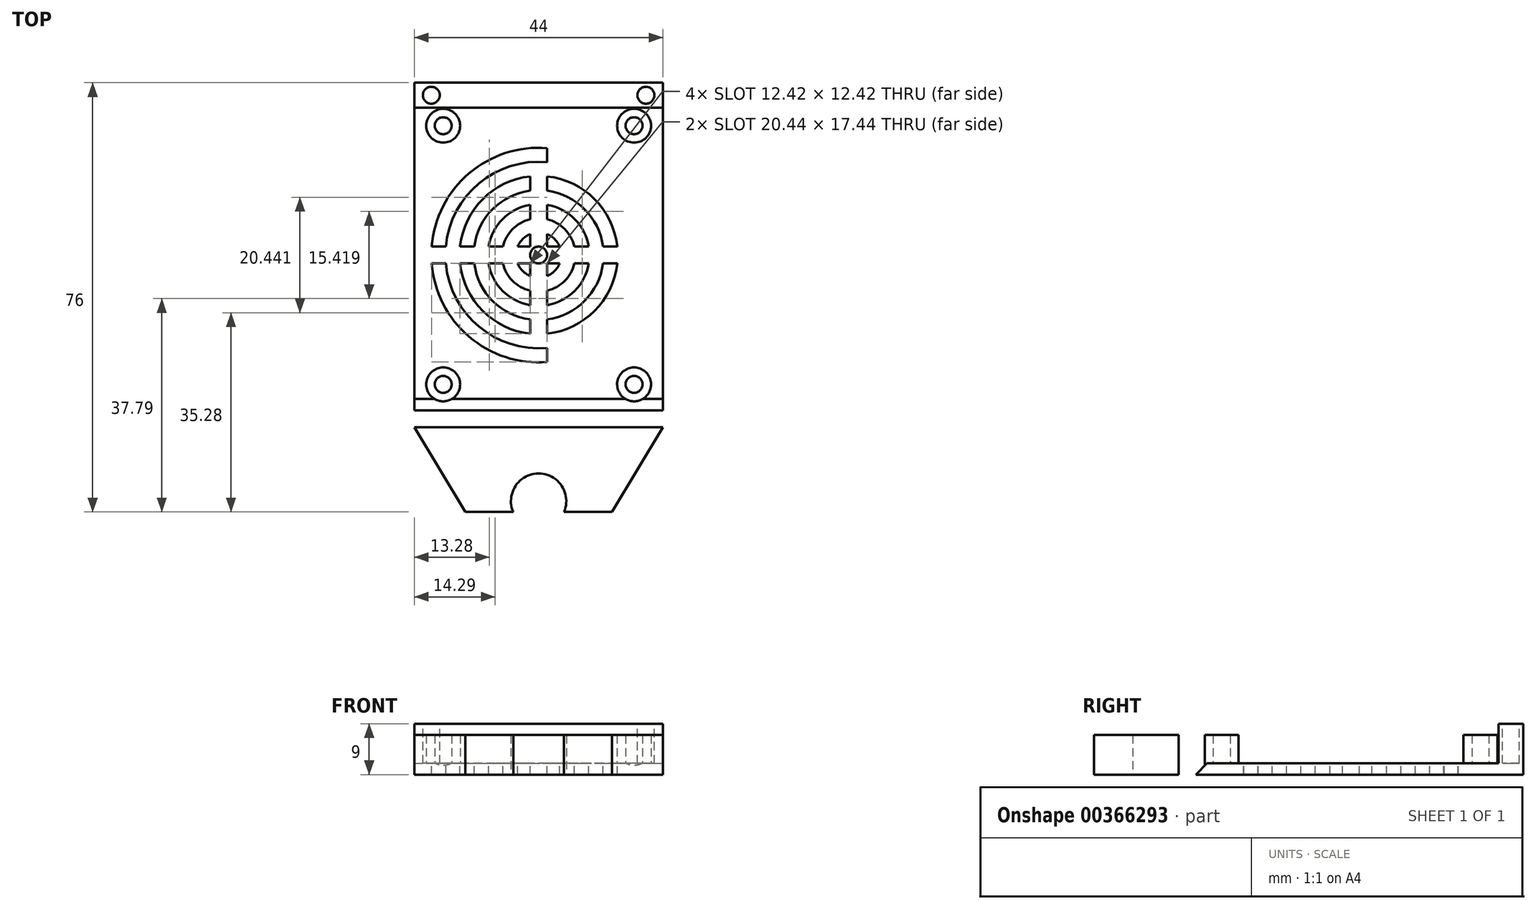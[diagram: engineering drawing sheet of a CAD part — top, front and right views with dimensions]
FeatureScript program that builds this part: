
annotation { "Feature Type Name" : "Feature", "Feature Type Description" : "" }
export const myFeature = defineFeature(function(context is Context, id is Id, definition is map)
    precondition{}
    {
        {
            var Q0;
            Q0=qCreatedBy(makeId("Top.planeOp"),FACE);
            var sketch = newSketch(context, id + "F0", { "sketchPlane" : qUnion([Q0])});
            skLineSegment(sketch, "E0.bottom", {"start": v(22, -30.5) * mm, "end": v(-22, -30.5) * mm});
            skLineSegment(sketch, "E0.top", {"start": v(22, 30.5) * mm, "end": v(-22, 30.5) * mm});
            skLineSegment(sketch, "E0.left", {"start": v(22, -30.5) * mm, "end": v(22, 30.5) * mm});
            skLineSegment(sketch, "E0.right", {"start": v(-22, -30.5) * mm, "end": v(-22, 30.5) * mm});
            skPoint(sketch, "E0.middle", {"position": v(0, 0) * mm});
            skSolve(sketch);
        }
        {
            var Q0;
            Q0=makeQuery(id+"F0.imprint","IMPRINT",FACE,{"disambiguationData":[TD([[makeQuery(id+"F0.imprint","IMPRINT",EDGE,{"derivedFrom":sQuery(id+"F0.wireOp",EDGE,"E0.bottom")}),-1.0]])]});
            extrude(context, id + "F1", {"entities" : qUnion([Q0]), "depth" : 2 * mm});
        }
        {
            var Q0;
            Q0=makeQuery(id+"F1.opExtrude","CAP_FACE",FACE,{"disambiguationData":[OSD([sQuery(id+"F0.wireOp",EDGE,"E0.bottom"),sQuery(id+"F0.wireOp",EDGE,"E0.top"),sQuery(id+"F0.wireOp",EDGE,"E0.left"),sQuery(id+"F0.wireOp",EDGE,"E0.right")])],"isStart":true});
            var sketch = newSketch(context, id + "F2", { "sketchPlane" : qUnion([Q0])});
            skLineSegment(sketch, "E1", {"start": v(-22, 30.5) * mm, "end": v(-13.01, 45.5) * mm});
            skLineSegment(sketch, "E2", {"start": v(-13.01, 45.5) * mm, "end": v(13.01, 45.5) * mm});
            skLineSegment(sketch, "E3", {"start": v(13.01, 45.5) * mm, "end": v(22, 30.5) * mm});
            skPoint(sketch, "E4", {"position": v(0, 45.5) * mm});
            skArc(sketch, "E5", {"start": v(4.5, 45.5) * mm, "mid": v(0, 38.66) * mm, "end": v(-4.5, 45.5) * mm});
            skSolve(sketch);
        }
        {
            var Q0;
            {var subQ3=sQuery(id+"F2.wireOp",EDGE,"E1");Q0=makeQuery(id+"F2.imprint","IMPRINT",FACE,{"disambiguationData":[TD([[makeQuery(id+"F2.imprint","IMPRINT",EDGE,{"derivedFrom":subQ3}),-1.0]])]});}
            extrude(context, id + "F3", {"entities" : qUnion([Q0]), "oppositeDirection" : true, "depth" : 7 * mm});
        }
        {
            var Q0;
            Q0=makeQuery(id+"F1.opExtrude","CAP_FACE",FACE,{"disambiguationData":[OSD([sQuery(id+"F0.wireOp",EDGE,"E0.bottom"),sQuery(id+"F0.wireOp",EDGE,"E0.top"),sQuery(id+"F0.wireOp",EDGE,"E0.left"),sQuery(id+"F0.wireOp",EDGE,"E0.right")])],"isStart":false});
            var sketch = newSketch(context, id + "F4", { "sketchPlane" : qUnion([Q0])});
            skCircle(sketch, "E6", {"center": v(-16.9, 22.9) * mm, "radius": 3 * mm});
            skCircle(sketch, "E7", {"center": v(16.9, 22.9) * mm, "radius": 3 * mm});
            skCircle(sketch, "E8", {"center": v(-16.9, -22.9) * mm, "radius": 3 * mm});
            skCircle(sketch, "E9", {"center": v(16.9, -22.9) * mm, "radius": 3 * mm});
            skCircle(sketch, "E10", {"center": v(-16.9, 22.9) * mm, "radius": 1.5 * mm});
            skCircle(sketch, "E11", {"center": v(16.9, 22.9) * mm, "radius": 1.5 * mm});
            skCircle(sketch, "E12", {"center": v(16.9, -22.9) * mm, "radius": 1.5 * mm});
            skCircle(sketch, "E13", {"center": v(-16.9, -22.9) * mm, "radius": 1.5 * mm});
            skSolve(sketch);
        }
        {
            var Q0;
            Q0=makeQuery(id+"F4.imprint","IMPRINT",FACE,{"disambiguationData":[TD([[makeQuery(id+"F4.imprint","IMPRINT",EDGE,{"derivedFrom":sQuery(id+"F4.wireOp",EDGE,"E6")}),1.0]])]});
            var Q1;
            Q1=makeQuery(id+"F4.imprint","IMPRINT",FACE,{"disambiguationData":[TD([[makeQuery(id+"F4.imprint","IMPRINT",EDGE,{"derivedFrom":sQuery(id+"F4.wireOp",EDGE,"E7")}),1.0]])]});
            var Q2;
            Q2=makeQuery(id+"F4.imprint","IMPRINT",FACE,{"disambiguationData":[TD([[makeQuery(id+"F4.imprint","IMPRINT",EDGE,{"derivedFrom":sQuery(id+"F4.wireOp",EDGE,"E9")}),1.0]])]});
            var Q3;
            Q3=makeQuery(id+"F4.imprint","IMPRINT",FACE,{"disambiguationData":[TD([[makeQuery(id+"F4.imprint","IMPRINT",EDGE,{"derivedFrom":sQuery(id+"F4.wireOp",EDGE,"E8")}),1.0]])]});
            extrude(context, id + "F5", {"entities" : qUnion([Q0, Q1, Q2, Q3]), "operationType" : NewBodyOperationType.ADD, "depth" : 5 * mm});
        }
        {
            var Q0;
            Q0=makeQuery(id+"F1.opExtrude","CAP_EDGE",EDGE,{"disambiguationData":[OSD([sQuery(id+"F0.wireOp",EDGE,"E0.bottom")])],"isStart":false});
            chamfer(context, id + "F6", {"entities" : qUnion([Q0]), "width" : 5 * mm, "tangentPropagation" : true});
        }
        {
            var Q0;
            {var subQ0=sQuery(id+"F0.wireOp",EDGE,"E0.left");var subQ1=sQuery(id+"F0.wireOp",EDGE,"E0.top");var subQ2=sQuery(id+"F0.wireOp",EDGE,"E0.right");var subQ3=sQuery(id+"F0.wireOp",EDGE,"E0.bottom");Q0=makeQuery(id+"F5.boolean.opBoolean","SPLIT",FACE,{"disambiguationData":[TD([makeQuery(id+"F1.opExtrude","SWEPT_FACE",FACE,{"disambiguationData":[OSD([subQ3])]})])],"derivedFrom":makeQuery(id+"F1.opExtrude","CAP_FACE",FACE,{"disambiguationData":[OSD([subQ3,subQ1,subQ0,subQ2])],"isStart":false})});}
            var sketch = newSketch(context, id + "F7", { "sketchPlane" : qUnion([Q0])});
            skLineSegment(sketch, "E14.bottom", {"start": v(-22, 30.5) * mm, "end": v(22, 30.5) * mm});
            skLineSegment(sketch, "E14.top", {"start": v(-22, 26.1) * mm, "end": v(22, 26.1) * mm});
            skLineSegment(sketch, "E14.left", {"start": v(-22, 30.5) * mm, "end": v(-22, 26.1) * mm});
            skLineSegment(sketch, "E14.right", {"start": v(22, 30.5) * mm, "end": v(22, 26.1) * mm});
            skSolve(sketch);
        }
        {
            var Q0;
            Q0=makeQuery(id+"F7.imprint","IMPRINT",FACE,{"disambiguationData":[TD([[makeQuery(id+"F7.imprint","IMPRINT",EDGE,{"derivedFrom":sQuery(id+"F7.wireOp",EDGE,"E14.bottom")}),1.0]])]});
            extrude(context, id + "F8", {"entities" : qUnion([Q0]), "operationType" : NewBodyOperationType.ADD, "depth" : 7 * mm});
        }
        {
            var Q0;
            Q0=makeQuery(id+"F8.opExtrude","CAP_FACE",FACE,{"disambiguationData":[OSD([sQuery(id+"F7.wireOp",EDGE,"E14.bottom"),sQuery(id+"F7.wireOp",EDGE,"E14.top"),sQuery(id+"F7.wireOp",EDGE,"E14.left"),sQuery(id+"F7.wireOp",EDGE,"E14.right")])],"isStart":false});
            var sketch = newSketch(context, id + "F9", { "sketchPlane" : qUnion([Q0])});
            skCircle(sketch, "E15", {"center": v(-19, 28.3) * mm, "radius": 1.5 * mm});
            skCircle(sketch, "E16", {"center": v(19, 28.3) * mm, "radius": 1.5 * mm});
            skPoint(sketch, "E17", {"position": v(22, 28.3) * mm});
            skSolve(sketch);
        }
        {
            var Q0;
            Q0=makeQuery(id+"F9.imprint","IMPRINT",FACE,{"disambiguationData":[TD([[makeQuery(id+"F9.imprint","IMPRINT",EDGE,{"derivedFrom":sQuery(id+"F9.wireOp",EDGE,"E15")}),1.0]])]});
            var Q1;
            Q1=makeQuery(id+"F9.imprint","IMPRINT",FACE,{"disambiguationData":[TD([[makeQuery(id+"F9.imprint","IMPRINT",EDGE,{"derivedFrom":sQuery(id+"F9.wireOp",EDGE,"E16")}),1.0]])]});
            extrude(context, id + "F10", {"entities" : qUnion([Q0, Q1]), "operationType" : NewBodyOperationType.REMOVE, "oppositeDirection" : true, "depth" : 7 * mm});
        }
        {
            var Q0;
            {var subQ0=sQuery(id+"F0.wireOp",EDGE,"E0.left");var subQ1=sQuery(id+"F0.wireOp",EDGE,"E0.top");var subQ2=sQuery(id+"F0.wireOp",EDGE,"E0.right");var subQ3=sQuery(id+"F0.wireOp",EDGE,"E0.bottom");Q0=makeQuery(id+"F5.boolean.opBoolean","SPLIT",FACE,{"disambiguationData":[TD([makeQuery(id+"F1.opExtrude","SWEPT_FACE",FACE,{"disambiguationData":[OSD([subQ3])]})])],"derivedFrom":makeQuery(id+"F1.opExtrude","CAP_FACE",FACE,{"disambiguationData":[OSD([subQ3,subQ1,subQ0,subQ2])],"isStart":false})});}
            var sketch = newSketch(context, id + "F11", { "sketchPlane" : qUnion([Q0])});
            skCircle(sketch, "E18", {"center": v(0, 0) * mm, "radius": 19 * mm});
            skCircle(sketch, "E19", {"center": v(0, 0) * mm, "radius": 16.5 * mm});
            skCircle(sketch, "E20", {"center": v(0, 0) * mm, "radius": 14 * mm});
            skCircle(sketch, "E21", {"center": v(0, 0) * mm, "radius": 11.5 * mm});
            skCircle(sketch, "E22", {"center": v(0, 0) * mm, "radius": 9 * mm});
            skCircle(sketch, "E23", {"center": v(0, 0) * mm, "radius": 6.5 * mm});
            skCircle(sketch, "E24", {"center": v(0, 0) * mm, "radius": 4 * mm});
            skCircle(sketch, "E25", {"center": v(0, 0) * mm, "radius": 1.5 * mm});
            skLineSegment(sketch, "E26", {"start": v(-1.5, 18.94) * mm, "end": v(-1.5, -18.94) * mm});
            skLineSegment(sketch, "E27", {"start": v(1.5, -18.94) * mm, "end": v(1.5, 18.94) * mm});
            skLineSegment(sketch, "E28", {"start": v(-18.94, 1.5) * mm, "end": v(18.94, 1.5) * mm});
            skLineSegment(sketch, "E29", {"start": v(-18.94, -1.5) * mm, "end": v(18.94, -1.5) * mm});
            skSolve(sketch);
        }
        {
            var Q0;
            {var subQ0=sQuery(id+"F11.wireOp",EDGE,"E26");var subQ1=sQuery(id+"F11.wireOp",EDGE,"E18");var subQ2=makeQuery(id+"F11.imprint","INTERSECT",VERTEX,{"disambiguationData":[OD(0.0)],"derivedFrom":[subQ1,subQ0]});Q0=makeQuery(id+"F11.imprint","IMPRINT",FACE,{"disambiguationData":[TD([[makeQuery(id+"F11.imprint","IMPRINT",EDGE,{"disambiguationData":[TD([[subQ2,-1.0]])],"derivedFrom":subQ1}),1.0]])]});}
            var Q1;
            {var subQ0=sQuery(id+"F11.wireOp",EDGE,"E27");var subQ1=sQuery(id+"F11.wireOp",EDGE,"E18");var subQ2=makeQuery(id+"F11.imprint","INTERSECT",VERTEX,{"disambiguationData":[OD(1.0)],"derivedFrom":[subQ1,subQ0]});Q1=makeQuery(id+"F11.imprint","IMPRINT",FACE,{"disambiguationData":[TD([[makeQuery(id+"F11.imprint","IMPRINT",EDGE,{"disambiguationData":[TD([[subQ2,1.0]])],"derivedFrom":subQ1}),1.0]])]});}
            var Q2;
            {var subQ0=sQuery(id+"F11.wireOp",EDGE,"E27");var subQ1=sQuery(id+"F11.wireOp",EDGE,"E18");var subQ2=makeQuery(id+"F11.imprint","INTERSECT",VERTEX,{"disambiguationData":[OD(0.0)],"derivedFrom":[subQ1,subQ0]});Q2=makeQuery(id+"F11.imprint","IMPRINT",FACE,{"disambiguationData":[TD([[makeQuery(id+"F11.imprint","IMPRINT",EDGE,{"disambiguationData":[TD([[subQ2,-1.0]])],"derivedFrom":subQ1}),1.0]])]});}
            var Q3;
            {var subQ0=sQuery(id+"F11.wireOp",EDGE,"E26");var subQ1=sQuery(id+"F11.wireOp",EDGE,"E18");var subQ2=makeQuery(id+"F11.imprint","INTERSECT",VERTEX,{"disambiguationData":[OD(1.0)],"derivedFrom":[subQ1,subQ0]});Q3=makeQuery(id+"F11.imprint","IMPRINT",FACE,{"disambiguationData":[TD([[makeQuery(id+"F11.imprint","IMPRINT",EDGE,{"disambiguationData":[TD([[subQ2,1.0]])],"derivedFrom":subQ1}),1.0]])]});}
            var Q4;
            {var subQ0=sQuery(id+"F11.wireOp",EDGE,"E29");var subQ1=sQuery(id+"F11.wireOp",EDGE,"E20");var subQ2=makeQuery(id+"F11.imprint","INTERSECT",VERTEX,{"disambiguationData":[OD(0.0)],"derivedFrom":[subQ1,subQ0]});Q4=makeQuery(id+"F11.imprint","IMPRINT",FACE,{"disambiguationData":[TD([[makeQuery(id+"F11.imprint","IMPRINT",EDGE,{"disambiguationData":[TD([[subQ2,-1.0]])],"derivedFrom":subQ1}),1.0]])]});}
            var Q5;
            {var subQ0=sQuery(id+"F11.wireOp",EDGE,"E29");var subQ1=sQuery(id+"F11.wireOp",EDGE,"E22");var subQ2=makeQuery(id+"F11.imprint","INTERSECT",VERTEX,{"disambiguationData":[OD(0.0)],"derivedFrom":[subQ1,subQ0]});Q5=makeQuery(id+"F11.imprint","IMPRINT",FACE,{"disambiguationData":[TD([[makeQuery(id+"F11.imprint","IMPRINT",EDGE,{"disambiguationData":[TD([[subQ2,-1.0]])],"derivedFrom":subQ1}),1.0]])]});}
            var Q6;
            {var subQ0=sQuery(id+"F11.wireOp",EDGE,"E27");var subQ1=sQuery(id+"F11.wireOp",EDGE,"E20");var subQ2=makeQuery(id+"F11.imprint","INTERSECT",VERTEX,{"disambiguationData":[OD(1.0)],"derivedFrom":[subQ1,subQ0]});Q6=makeQuery(id+"F11.imprint","IMPRINT",FACE,{"disambiguationData":[TD([[makeQuery(id+"F11.imprint","IMPRINT",EDGE,{"disambiguationData":[TD([[subQ2,-1.0]])],"derivedFrom":subQ1}),1.0]])]});}
            var Q7;
            {var subQ0=sQuery(id+"F11.wireOp",EDGE,"E27");var subQ1=sQuery(id+"F11.wireOp",EDGE,"E22");var subQ2=makeQuery(id+"F11.imprint","INTERSECT",VERTEX,{"disambiguationData":[OD(1.0)],"derivedFrom":[subQ1,subQ0]});Q7=makeQuery(id+"F11.imprint","IMPRINT",FACE,{"disambiguationData":[TD([[makeQuery(id+"F11.imprint","IMPRINT",EDGE,{"disambiguationData":[TD([[subQ2,-1.0]])],"derivedFrom":subQ1}),1.0]])]});}
            var Q8;
            {var subQ0=sQuery(id+"F11.wireOp",EDGE,"E27");var subQ1=sQuery(id+"F11.wireOp",EDGE,"E20");var subQ2=makeQuery(id+"F11.imprint","INTERSECT",VERTEX,{"disambiguationData":[OD(0.0)],"derivedFrom":[subQ1,subQ0]});Q8=makeQuery(id+"F11.imprint","IMPRINT",FACE,{"disambiguationData":[TD([[makeQuery(id+"F11.imprint","IMPRINT",EDGE,{"disambiguationData":[TD([[subQ2,1.0]])],"derivedFrom":subQ1}),1.0]])]});}
            var Q9;
            {var subQ0=sQuery(id+"F11.wireOp",EDGE,"E27");var subQ1=sQuery(id+"F11.wireOp",EDGE,"E22");var subQ2=makeQuery(id+"F11.imprint","INTERSECT",VERTEX,{"disambiguationData":[OD(0.0)],"derivedFrom":[subQ1,subQ0]});Q9=makeQuery(id+"F11.imprint","IMPRINT",FACE,{"disambiguationData":[TD([[makeQuery(id+"F11.imprint","IMPRINT",EDGE,{"disambiguationData":[TD([[subQ2,1.0]])],"derivedFrom":subQ1}),1.0]])]});}
            var Q10;
            {var subQ0=sQuery(id+"F11.wireOp",EDGE,"E26");var subQ1=sQuery(id+"F11.wireOp",EDGE,"E20");var subQ2=makeQuery(id+"F11.imprint","INTERSECT",VERTEX,{"disambiguationData":[OD(0.0)],"derivedFrom":[subQ1,subQ0]});Q10=makeQuery(id+"F11.imprint","IMPRINT",FACE,{"disambiguationData":[TD([[makeQuery(id+"F11.imprint","IMPRINT",EDGE,{"disambiguationData":[TD([[subQ2,-1.0]])],"derivedFrom":subQ1}),1.0]])]});}
            var Q11;
            {var subQ0=sQuery(id+"F11.wireOp",EDGE,"E26");var subQ1=sQuery(id+"F11.wireOp",EDGE,"E22");var subQ2=makeQuery(id+"F11.imprint","INTERSECT",VERTEX,{"disambiguationData":[OD(0.0)],"derivedFrom":[subQ1,subQ0]});Q11=makeQuery(id+"F11.imprint","IMPRINT",FACE,{"disambiguationData":[TD([[makeQuery(id+"F11.imprint","IMPRINT",EDGE,{"disambiguationData":[TD([[subQ2,-1.0]])],"derivedFrom":subQ1}),1.0]])]});}
            var Q12;
            {var subQ0=sQuery(id+"F11.wireOp",EDGE,"E26");var subQ1=sQuery(id+"F11.wireOp",EDGE,"E24");var subQ2=makeQuery(id+"F11.imprint","INTERSECT",VERTEX,{"disambiguationData":[OD(0.0)],"derivedFrom":[subQ1,subQ0]});Q12=makeQuery(id+"F11.imprint","IMPRINT",FACE,{"disambiguationData":[TD([[makeQuery(id+"F11.imprint","IMPRINT",EDGE,{"disambiguationData":[TD([[subQ2,-1.0]])],"derivedFrom":subQ1}),1.0]])]});}
            var Q13;
            {var subQ0=sQuery(id+"F11.wireOp",EDGE,"E27");var subQ1=sQuery(id+"F11.wireOp",EDGE,"E24");var subQ2=makeQuery(id+"F11.imprint","INTERSECT",VERTEX,{"disambiguationData":[OD(0.0)],"derivedFrom":[subQ1,subQ0]});Q13=makeQuery(id+"F11.imprint","IMPRINT",FACE,{"disambiguationData":[TD([[makeQuery(id+"F11.imprint","IMPRINT",EDGE,{"disambiguationData":[TD([[subQ2,1.0]])],"derivedFrom":subQ1}),1.0]])]});}
            var Q14;
            {var subQ0=sQuery(id+"F11.wireOp",EDGE,"E27");var subQ1=sQuery(id+"F11.wireOp",EDGE,"E24");var subQ2=makeQuery(id+"F11.imprint","INTERSECT",VERTEX,{"disambiguationData":[OD(1.0)],"derivedFrom":[subQ1,subQ0]});Q14=makeQuery(id+"F11.imprint","IMPRINT",FACE,{"disambiguationData":[TD([[makeQuery(id+"F11.imprint","IMPRINT",EDGE,{"disambiguationData":[TD([[subQ2,-1.0]])],"derivedFrom":subQ1}),1.0]])]});}
            var Q15;
            {var subQ0=sQuery(id+"F11.wireOp",EDGE,"E29");var subQ1=sQuery(id+"F11.wireOp",EDGE,"E24");var subQ2=makeQuery(id+"F11.imprint","INTERSECT",VERTEX,{"disambiguationData":[OD(0.0)],"derivedFrom":[subQ1,subQ0]});Q15=makeQuery(id+"F11.imprint","IMPRINT",FACE,{"disambiguationData":[TD([[makeQuery(id+"F11.imprint","IMPRINT",EDGE,{"disambiguationData":[TD([[subQ2,-1.0]])],"derivedFrom":subQ1}),1.0]])]});}
            var Q16;
            {var subQ0=sQuery(id+"F11.wireOp",EDGE,"E25");var subQ1=makeQuery(id+"F11.imprint","INTERSECT",VERTEX,{"derivedFrom":[subQ0,sQuery(id+"F11.wireOp",EDGE,"E28")]});Q16=makeQuery(id+"F11.imprint","IMPRINT",FACE,{"disambiguationData":[TD([[makeQuery(id+"F11.imprint","IMPRINT",EDGE,{"disambiguationData":[TD([[subQ1,1.0]])],"derivedFrom":subQ0}),1.0]])]});}
            extrude(context, id + "F12", {"entities" : qUnion([Q0, Q1, Q2, Q3, Q4, Q5, Q6, Q7, Q8, Q9, Q10, Q11, Q12, Q13, Q14, Q15, Q16]), "operationType" : NewBodyOperationType.REMOVE, "endBound" : BoundingType.THROUGH_ALL, "oppositeDirection" : true, "depth" : 25 * mm});
        }
    });
